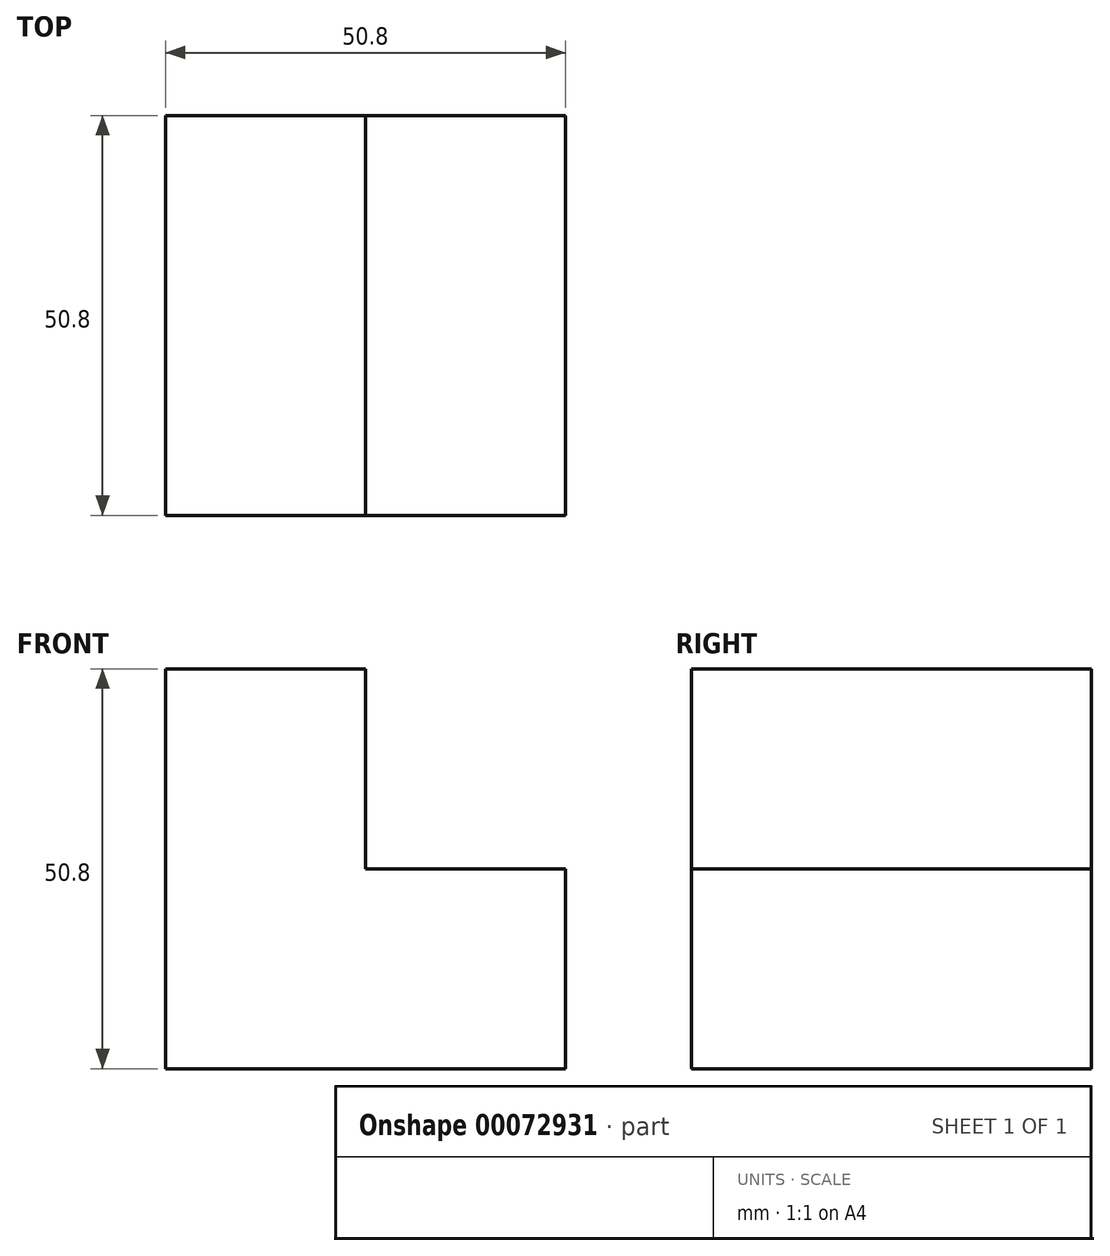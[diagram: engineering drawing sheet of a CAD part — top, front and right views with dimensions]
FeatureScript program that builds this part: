
annotation { "Feature Type Name" : "Feature", "Feature Type Description" : "" }
export const myFeature = defineFeature(function(context is Context, id is Id, definition is map)
    precondition{}
    {
        {
            var Q0;
            Q0=qCreatedBy(makeId("Front.planeOp"),FACE);
            var sketch = newSketch(context, id + "F0", { "sketchPlane" : qUnion([Q0])});
            skLineSegment(sketch, "E0", {"start": v(0, 0) * mm, "end": v(25.4, 0) * mm});
            skLineSegment(sketch, "E1", {"start": v(25.4, 0) * mm, "end": v(25.4, -25.4) * mm});
            skLineSegment(sketch, "E2", {"start": v(25.4, -25.4) * mm, "end": v(-25.4, -25.4) * mm});
            skLineSegment(sketch, "E3", {"start": v(-25.4, -25.4) * mm, "end": v(-25.4, 25.4) * mm});
            skLineSegment(sketch, "E4", {"start": v(-25.4, 25.4) * mm, "end": v(0, 25.4) * mm});
            skLineSegment(sketch, "E5", {"start": v(0, 25.4) * mm, "end": v(0, 0) * mm});
            skSolve(sketch);
        }
        {
            var Q0;
            Q0 = qSketchRegion(id + "F0", true);
            extrude(context, id + "F1", {"entities" : qUnion([Q0]), "depth" : 25.4 * mm, "hasSecondDirection" : true, "secondDirectionOppositeDirection" : true, "secondDirectionDepth" : 25.4 * mm});
        }
    });
